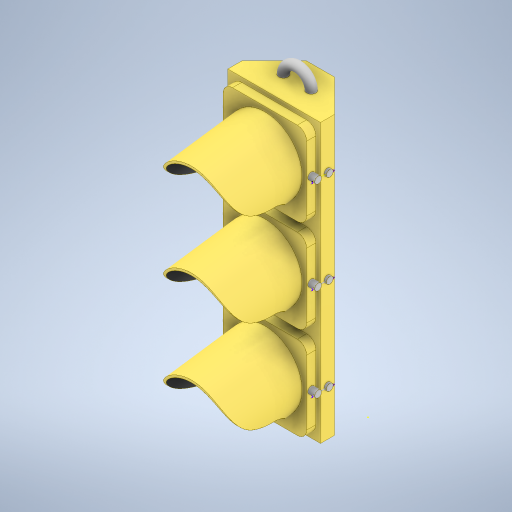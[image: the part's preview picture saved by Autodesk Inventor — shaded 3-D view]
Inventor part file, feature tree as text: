
AUTODESK INVENTOR PART (.ipt)
format: ipt  version: 2023.3 (Build 273359000, 359)  size: 486,400 bytes
history: mixed  units: in
note: dims shown in document units (in); Inventor stores cm internally (conversion verified against a paired STEP export)
features: sketch x6, sweep x6, extrude x1, plane x1, imported_body x1
ambient origin geometry x8: Origin, YZ Plane, XZ Plane, XY Plane, X Axis, Y Axis, Z Axis, Center Point
bodies: Solid2 (imported_parasolid), Solid1 (imported_parasolid)
feature tree (15):
  extrude  "Extrusion1"  Depth=0.08in
  plane  "Work Plane1"
  sketch  "Sketch3"  dims[d5=0.625in d6=0.0in d7=0.0in]
  sketch  "Sketch2"  dims[d2=0.08in d3=2.25in d4=0.0in]
  sweep  "Sweep1"
  sweep  "Sweep2"
  sweep  "Sweep3"
  sweep  "Sweep4"
  sweep  "Sweep5"
  sweep  "Sweep6"
  sketch  "Sketch1"  dims[d0=0.08in d1=0.08in]
  sketch  "Sketch4"  dims[d8=0.0in d9=0.0in d10=0.0in d11=0.0in]
  sketch  "Sketch5"  dims[d12=0.0in d13=0.0in d14=0.0in d15=0.0in]
  sketch  "Sketch6"  dims[d16=0.0in d17=0.0in]
  imported_body  NMx_Import_Brep_tag  [imported B-rep: ~14 faces, bbox_mm=[2.032035, 257.938707, 3.20057]]
